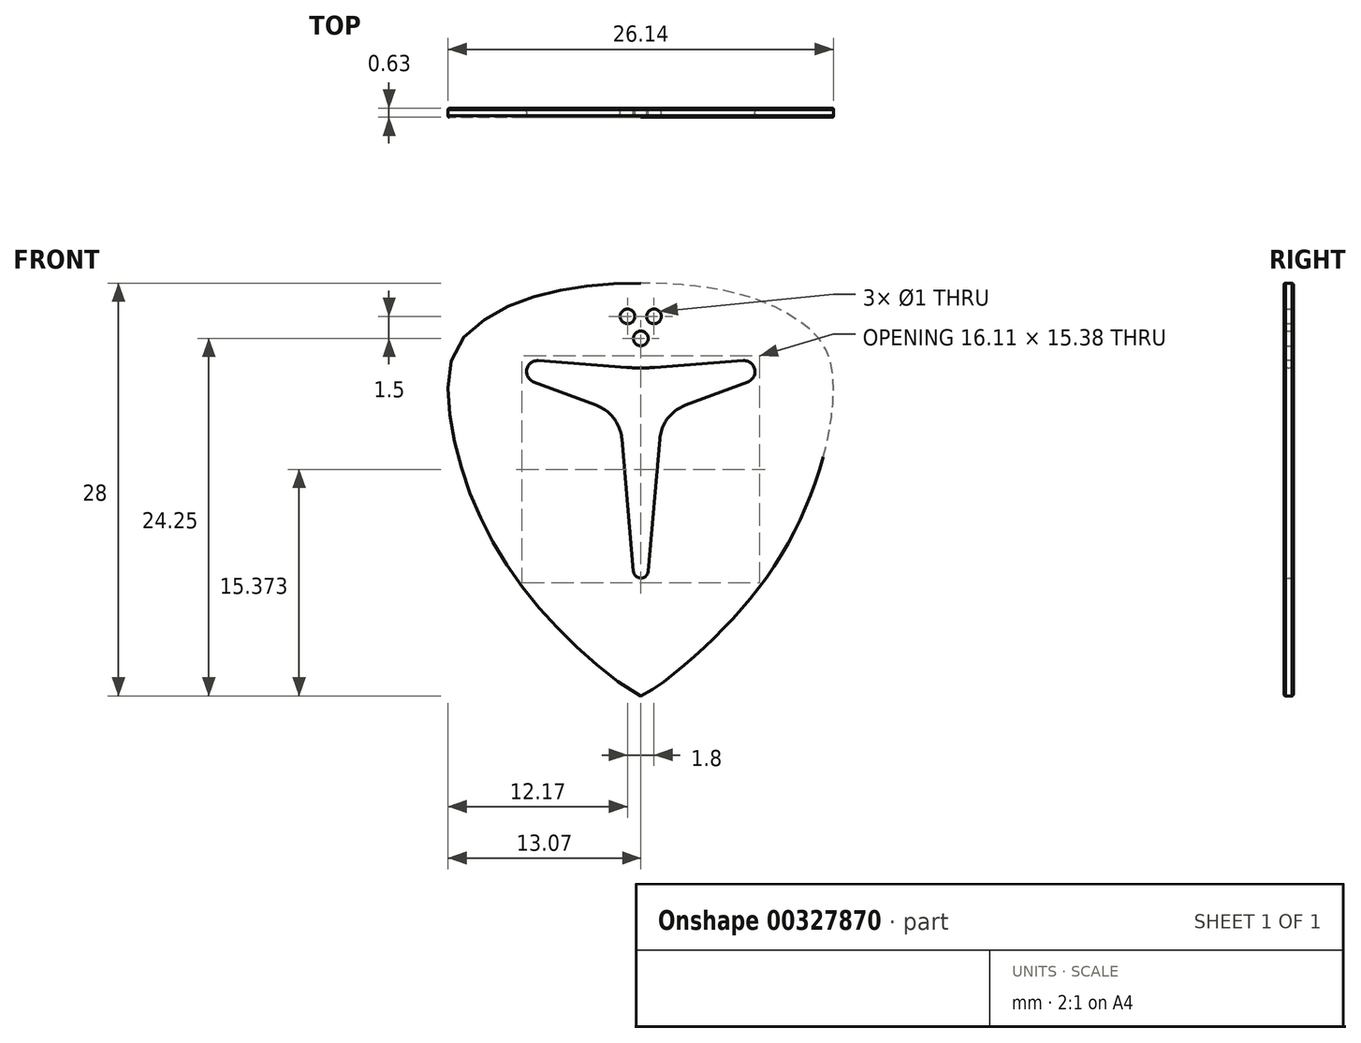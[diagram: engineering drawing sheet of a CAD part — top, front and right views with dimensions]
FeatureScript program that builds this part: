
annotation { "Feature Type Name" : "Feature", "Feature Type Description" : "" }
export const myFeature = defineFeature(function(context is Context, id is Id, definition is map)
    precondition{}
    {
        {
            var Q0;
            Q0=qCreatedBy(makeId("Front.planeOp"),FACE);
            var sketch = newSketch(context, id + "F0", { "sketchPlane" : qUnion([Q0])});
            skLineSegment(sketch, "E0", {"start": v(0, 0) * mm, "end": v(0, 6) * mm, "construction": true});
            skLineSegment(sketch, "E1", {"start": v(0, 0) * mm, "end": v(0, -22) * mm, "construction": true});
            skLineSegment(sketch, "E2", {"start": v(0, 0) * mm, "end": v(13, 0) * mm, "construction": true});
            skFitSpline(sketch, "E3", {"points": [v(0, -22) * mm, v(8.5, -14) * mm, v(13, 0) * mm, v(11, 3.25) * mm, v(0, 6) * mm], "startDerivative": vector(5.52, 0) * mm, "endDerivative": vector(-67.2, 0) * mm});
            skFitSpline(sketch, "E4.MirrorCS", {"points": [v(0, -22) * mm, v(-8.5, -14) * mm, v(-13, 0) * mm, v(-11, 3.25) * mm, v(0, 6) * mm], "startDerivative": vector(-5.52, 0) * mm, "endDerivative": vector(67.2, 0) * mm});
            skArc(sketch, "E5", {"start": v(7.26, -0.7) * mm, "mid": v(7.73, 0.16) * mm, "end": v(6.94, 0.75) * mm});
            skLineSegment(sketch, "E6", {"start": v(7.26, -0.7) * mm, "end": v(3.04, -2.27) * mm});
            skArc(sketch, "E7", {"start": v(3.04, -2.27) * mm, "mid": v(1.83, -3.17) * mm, "end": v(1.28, -4.58) * mm});
            skLineSegment(sketch, "E8", {"start": v(0.5, -13.54) * mm, "end": v(1.28, -4.58) * mm});
            skArc(sketch, "E9", {"start": v(0, -14) * mm, "mid": v(0.34, -13.87) * mm, "end": v(0.5, -13.54) * mm});
            skArc(sketch, "E10.MirrorCS", {"start": v(0, -14) * mm, "mid": v(-0.34, -13.87) * mm, "end": v(-0.5, -13.54) * mm});
            skLineSegment(sketch, "E11.MirrorCS", {"start": v(-0.5, -13.54) * mm, "end": v(-1.28, -4.58) * mm});
            skArc(sketch, "E12.MirrorCS", {"start": v(-3.04, -2.27) * mm, "mid": v(-1.83, -3.17) * mm, "end": v(-1.28, -4.58) * mm});
            skLineSegment(sketch, "E13.MirrorCS", {"start": v(-7.26, -0.7) * mm, "end": v(-3.04, -2.27) * mm});
            skArc(sketch, "E14.MirrorCS", {"start": v(-7.26, -0.7) * mm, "mid": v(-7.73, 0.16) * mm, "end": v(-6.94, 0.75) * mm});
            skLineSegment(sketch, "E15", {"start": v(6.94, 0.75) * mm, "end": v(0.96, 0.29) * mm});
            skArc(sketch, "E16", {"start": v(0, 0.25) * mm, "mid": v(0.48, 0.26) * mm, "end": v(0.96, 0.29) * mm});
            skArc(sketch, "E17.MirrorCS", {"start": v(0, 0.25) * mm, "mid": v(-0.48, 0.26) * mm, "end": v(-0.96, 0.29) * mm});
            skLineSegment(sketch, "E18.MirrorCS", {"start": v(-6.94, 0.75) * mm, "end": v(-0.96, 0.29) * mm});
            skCircle(sketch, "E19", {"center": v(0, 2.25) * mm, "radius": 0.5 * mm});
            skCircle(sketch, "E20", {"center": v(0.9, 3.75) * mm, "radius": 0.5 * mm});
            skLineSegment(sketch, "E21", {"start": v(0.9, 3.75) * mm, "end": v(0, 3.75) * mm});
            skPoint(sketch, "E22", {"position": v(0, 3) * mm});
            skLineSegment(sketch, "E23.MirrorCS", {"start": v(-0.9, 3.75) * mm, "end": v(0, 3.75) * mm});
            skCircle(sketch, "E24.MirrorC", {"center": v(-0.9, 3.75) * mm, "radius": 0.5 * mm});
            skSolve(sketch);
        }
        {
            var Q0;
            Q0=qSketchRegion(id+"F0",true);
            extrude(context, id + "F1", {"entities" : qUnion([Q0]), "depth" : 0.63 * mm});
        }
        {
            var Q0;
            Q0=makeQuery(id+"F1.opExtrude","CAP_EDGE",EDGE,{"disambiguationData":[OSD([sQuery(id+"F0.wireOp",EDGE,"E5")])],"isStart":false});
            var Q1;
            Q1=makeQuery(id+"F1.opExtrude","CAP_EDGE",EDGE,{"disambiguationData":[OSD([sQuery(id+"F0.wireOp",EDGE,"E7")])],"isStart":true});
            var Q2;
            Q2=makeQuery(id+"F1.opExtrude","CAP_EDGE",EDGE,{"disambiguationData":[OSD([sQuery(id+"F0.wireOp",EDGE,"E9"),sQuery(id+"F0.wireOp",EDGE,"E10.MirrorCS")])],"isStart":false});
            var Q3;
            Q3=makeQuery(id+"F1.opExtrude","CAP_EDGE",EDGE,{"disambiguationData":[OSD([sQuery(id+"F0.wireOp",EDGE,"E14.MirrorCS")])],"isStart":false});
            var Q4;
            Q4=makeQuery(id+"F1.opExtrude","CAP_EDGE",EDGE,{"disambiguationData":[OSD([sQuery(id+"F0.wireOp",EDGE,"E5")])],"isStart":true});
            var Q5;
            Q5=makeQuery(id+"F1.opExtrude","CAP_EDGE",EDGE,{"disambiguationData":[OSD([sQuery(id+"F0.wireOp",EDGE,"E12.MirrorCS")])],"isStart":false});
            var Q6;
            Q6=makeQuery(id+"F1.opExtrude","CAP_EDGE",EDGE,{"disambiguationData":[OSD([sQuery(id+"F0.wireOp",EDGE,"E7")])],"isStart":false});
            var Q7;
            Q7=makeQuery(id+"F1.opExtrude","CAP_EDGE",EDGE,{"disambiguationData":[OSD([sQuery(id+"F0.wireOp",EDGE,"cP70XH3B-hxny-nh1n-TbyW-52Zl4TOD4HrO"),sQuery(id+"F0.wireOp",EDGE,"9cf6c757-e815-40dd-95a7-672993b90d513.MirrorCS")])],"isStart":true});
            var Q8;
            Q8=makeQuery(id+"F1.opExtrude","CAP_EDGE",EDGE,{"disambiguationData":[OSD([sQuery(id+"F0.wireOp",EDGE,"E13.MirrorCS")])],"isStart":false});
            var Q9;
            Q9=makeQuery(id+"F1.opExtrude","CAP_EDGE",EDGE,{"disambiguationData":[OSD([sQuery(id+"F0.wireOp",EDGE,"E12.MirrorCS")])],"isStart":true});
            var Q10;
            Q10=makeQuery(id+"F1.opExtrude","CAP_EDGE",EDGE,{"disambiguationData":[OSD([sQuery(id+"F0.wireOp",EDGE,"cP70XH3B-hxny-nh1n-TbyW-52Zl4TOD4HrO"),sQuery(id+"F0.wireOp",EDGE,"9cf6c757-e815-40dd-95a7-672993b90d513.MirrorCS")])],"isStart":false});
            var Q11;
            Q11=makeQuery(id+"F1.opExtrude","CAP_EDGE",EDGE,{"disambiguationData":[OSD([sQuery(id+"F0.wireOp",EDGE,"E9"),sQuery(id+"F0.wireOp",EDGE,"E10.MirrorCS")])],"isStart":true});
            var Q12;
            Q12=makeQuery(id+"F1.opExtrude","SWEPT_EDGE",EDGE,{"disambiguationData":[OSD([sQuery(id+"F0.wireOp",EDGE,"9cf6c757-e815-40dd-95a7-672993b90d513.MirrorCS"),sQuery(id+"F0.wireOp",EDGE,"E14.MirrorCS")])]});
            var Q13;
            Q13=makeQuery(id+"F1.opExtrude","CAP_EDGE",EDGE,{"disambiguationData":[OSD([sQuery(id+"F0.wireOp",EDGE,"E8")])],"isStart":true});
            var Q14;
            Q14=makeQuery(id+"F1.opExtrude","CAP_EDGE",EDGE,{"disambiguationData":[OSD([sQuery(id+"F0.wireOp",EDGE,"E11.MirrorCS")])],"isStart":false});
            var Q15;
            Q15=makeQuery(id+"F1.opExtrude","SWEPT_EDGE",EDGE,{"disambiguationData":[OSD([sQuery(id+"F0.wireOp",EDGE,"E6"),sQuery(id+"F0.wireOp",EDGE,"E7")])]});
            var Q16;
            Q16=makeQuery(id+"F1.opExtrude","SWEPT_EDGE",EDGE,{"disambiguationData":[OSD([sQuery(id+"F0.wireOp",EDGE,"E8"),sQuery(id+"F0.wireOp",EDGE,"E9")])]});
            var Q17;
            Q17=makeQuery(id+"F1.opExtrude","SWEPT_EDGE",EDGE,{"disambiguationData":[OSD([sQuery(id+"F0.wireOp",EDGE,"E13.MirrorCS"),sQuery(id+"F0.wireOp",EDGE,"E14.MirrorCS")])]});
            var Q18;
            Q18=makeQuery(id+"F1.opExtrude","SWEPT_EDGE",EDGE,{"disambiguationData":[OSD([sQuery(id+"F0.wireOp",EDGE,"E10.MirrorCS"),sQuery(id+"F0.wireOp",EDGE,"E11.MirrorCS")])]});
            var Q19;
            Q19=makeQuery(id+"F1.opExtrude","SWEPT_EDGE",EDGE,{"disambiguationData":[OSD([sQuery(id+"F0.wireOp",EDGE,"E11.MirrorCS"),sQuery(id+"F0.wireOp",EDGE,"E12.MirrorCS")])]});
            var Q20;
            Q20=makeQuery(id+"F1.opExtrude","SWEPT_EDGE",EDGE,{"disambiguationData":[OSD([sQuery(id+"F0.wireOp",EDGE,"E5"),sQuery(id+"F0.wireOp",EDGE,"E6")])]});
            var Q21;
            Q21=makeQuery(id+"F1.opExtrude","CAP_EDGE",EDGE,{"disambiguationData":[OSD([sQuery(id+"F0.wireOp",EDGE,"E14.MirrorCS")])],"isStart":true});
            var Q22;
            Q22=makeQuery(id+"F1.opExtrude","SWEPT_EDGE",EDGE,{"disambiguationData":[OSD([sQuery(id+"F0.wireOp",EDGE,"E12.MirrorCS"),sQuery(id+"F0.wireOp",EDGE,"E13.MirrorCS")])]});
            var Q23;
            Q23=makeQuery(id+"F1.opExtrude","CAP_EDGE",EDGE,{"disambiguationData":[OSD([sQuery(id+"F0.wireOp",EDGE,"E8")])],"isStart":false});
            var Q24;
            Q24=makeQuery(id+"F1.opExtrude","SWEPT_EDGE",EDGE,{"disambiguationData":[OSD([sQuery(id+"F0.wireOp",EDGE,"cP70XH3B-hxny-nh1n-TbyW-52Zl4TOD4HrO"),sQuery(id+"F0.wireOp",EDGE,"E5")])]});
            var Q25;
            Q25=makeQuery(id+"F1.opExtrude","CAP_EDGE",EDGE,{"disambiguationData":[OSD([sQuery(id+"F0.wireOp",EDGE,"E6")])],"isStart":false});
            var Q26;
            Q26=makeQuery(id+"F1.opExtrude","CAP_EDGE",EDGE,{"disambiguationData":[OSD([sQuery(id+"F0.wireOp",EDGE,"E11.MirrorCS")])],"isStart":true});
            var Q27;
            Q27=makeQuery(id+"F1.opExtrude","SWEPT_EDGE",EDGE,{"disambiguationData":[OSD([sQuery(id+"F0.wireOp",EDGE,"E7"),sQuery(id+"F0.wireOp",EDGE,"E8")])]});
            var Q28;
            Q28=makeQuery(id+"F1.opExtrude","CAP_EDGE",EDGE,{"disambiguationData":[OSD([sQuery(id+"F0.wireOp",EDGE,"E6")])],"isStart":true});
            var Q29;
            Q29=makeQuery(id+"F1.opExtrude","CAP_EDGE",EDGE,{"disambiguationData":[OSD([sQuery(id+"F0.wireOp",EDGE,"E13.MirrorCS")])],"isStart":true});
            var Q30;
            Q30=makeQuery(id+"F1.opExtrude","CAP_EDGE",EDGE,{"disambiguationData":[OSD([sQuery(id+"F0.wireOp",EDGE,"E18.MirrorCS")])],"isStart":false});
            var Q31;
            Q31=makeQuery(id+"F1.opExtrude","CAP_EDGE",EDGE,{"disambiguationData":[OSD([sQuery(id+"F0.wireOp",EDGE,"E18.MirrorCS")])],"isStart":true});
            var Q32;
            Q32=makeQuery(id+"F1.opExtrude","CAP_EDGE",EDGE,{"disambiguationData":[OSD([sQuery(id+"F0.wireOp",EDGE,"E16"),sQuery(id+"F0.wireOp",EDGE,"E17.MirrorCS")])],"isStart":false});
            var Q33;
            Q33=makeQuery(id+"F1.opExtrude","CAP_EDGE",EDGE,{"disambiguationData":[OSD([sQuery(id+"F0.wireOp",EDGE,"E16"),sQuery(id+"F0.wireOp",EDGE,"E17.MirrorCS")])],"isStart":true});
            var Q34;
            Q34=makeQuery(id+"F1.opExtrude","CAP_EDGE",EDGE,{"disambiguationData":[OSD([sQuery(id+"F0.wireOp",EDGE,"E15")])],"isStart":false});
            fillet(context, id + "F2", {"entities" : qUnion([Q0, Q1, Q2, Q3, Q4, Q5, Q6, Q7, Q8, Q9, Q10, Q11, Q12, Q13, Q14, Q15, Q16, Q17, Q18, Q19, Q20, Q21, Q22, Q23, Q24, Q25, Q26, Q27, Q28, Q29, Q30, Q31, Q32, Q33, Q34]), "radius" : (0.63 / 2) * mm, "tangentPropagation" : true, "allowEdgeOverflow" : false});
        }
        {
            var Q0;
            Q0=makeQuery(id+"F1.opExtrude","CAP_EDGE",EDGE,{"disambiguationData":[OSD([sQuery(id+"F0.wireOp",EDGE,"E3")])],"isStart":false});
            var Q1;
            Q1=makeQuery(id+"F1.opExtrude","CAP_EDGE",EDGE,{"disambiguationData":[OSD([sQuery(id+"F0.wireOp",EDGE,"E4.MirrorCS")])],"isStart":false});
            var Q2;
            Q2=makeQuery(id+"F1.opExtrude","CAP_EDGE",EDGE,{"disambiguationData":[OSD([sQuery(id+"F0.wireOp",EDGE,"E4.MirrorCS")])],"isStart":true});
            var Q3;
            Q3=makeQuery(id+"F1.opExtrude","CAP_EDGE",EDGE,{"disambiguationData":[OSD([sQuery(id+"F0.wireOp",EDGE,"E3")])],"isStart":true});
            fillet(context, id + "F3", {"entities" : qUnion([Q0, Q1, Q2, Q3]), "radius" : 0.1 * mm, "tangentPropagation" : true, "allowEdgeOverflow" : false});
        }
    });
